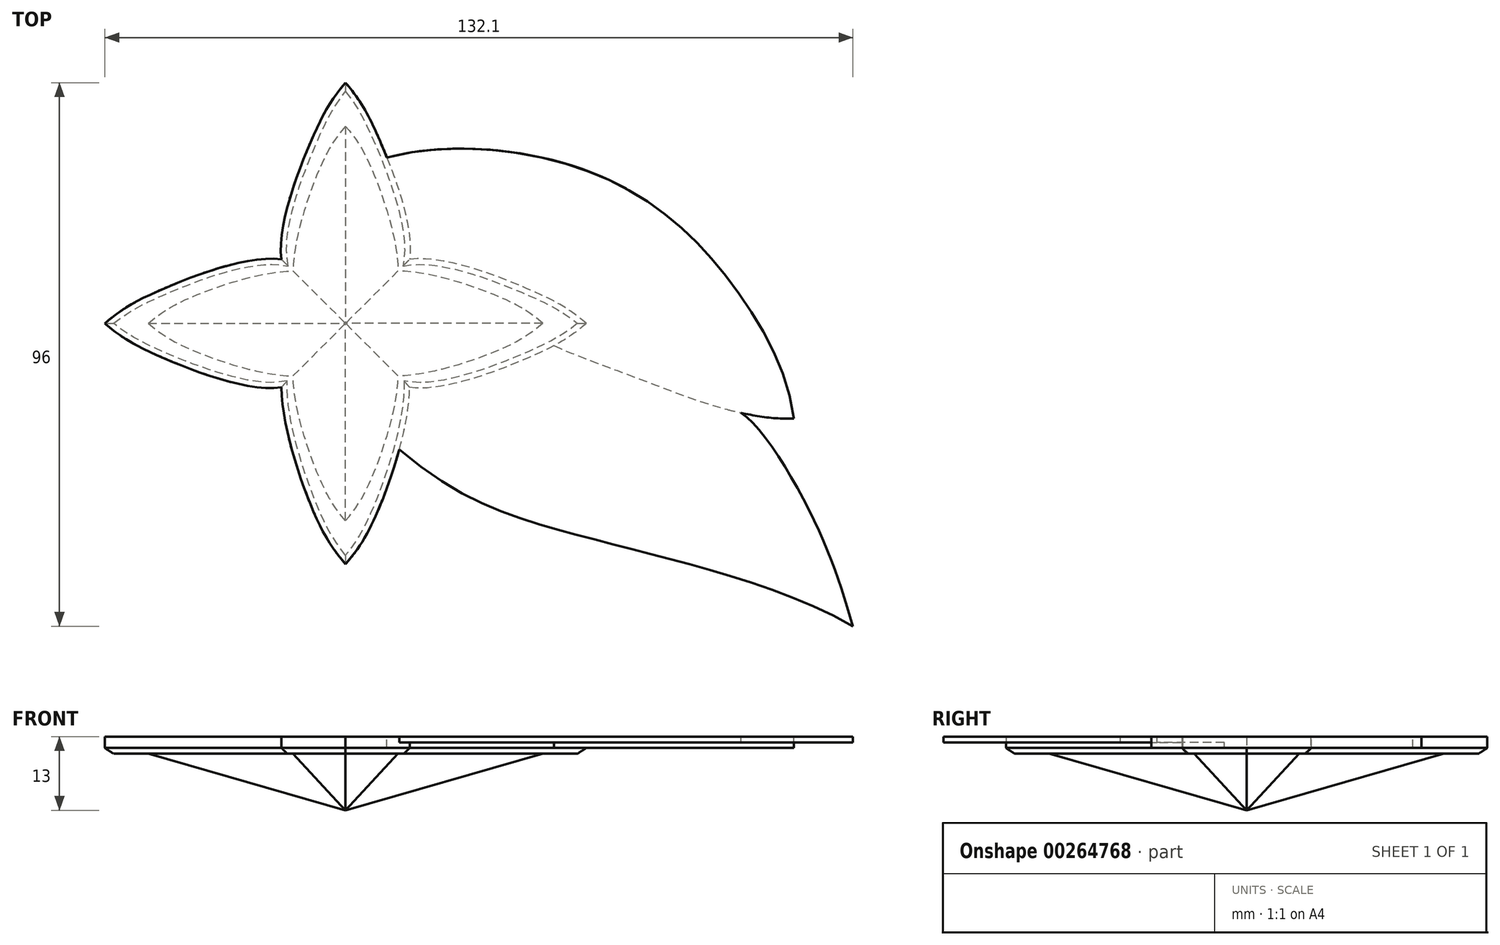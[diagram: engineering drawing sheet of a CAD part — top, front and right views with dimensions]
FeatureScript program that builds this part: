
annotation { "Feature Type Name" : "Feature", "Feature Type Description" : "" }
export const myFeature = defineFeature(function(context is Context, id is Id, definition is map)
    precondition{}
    {
        {
            var Q0;
            Q0=qCreatedBy(makeId("Top.planeOp"),FACE);
            var sketch = newSketch(context, id + "F0", { "sketchPlane" : qUnion([Q0])});
            skLineSegment(sketch, "E0", {"start": v(0, 0) * mm, "end": v(0, 50) * mm});
            skLineSegment(sketch, "E1", {"start": v(0, 0) * mm, "end": v(-50, 0) * mm});
            skFitSpline(sketch, "E2", {"points": [v(0, 50) * mm, v(-50, 0) * mm], "startDerivative": vector(-22.26, -93.04) * mm, "endDerivative": vector(-77.74, -6.96) * mm});
            skFitSpline(sketch, "E3.MirrorCS", {"points": [v(0, 50) * mm, v(50, 0) * mm], "startDerivative": vector(22.26, -93.04) * mm, "endDerivative": vector(77.74, -6.96) * mm});
            skFitSpline(sketch, "E4.MirrorCS", {"points": [v(0, -50) * mm, v(-50, 0) * mm], "startDerivative": vector(-22.26, 93.04) * mm, "endDerivative": vector(-77.74, 6.96) * mm});
            skFitSpline(sketch, "E5.MirrorCS", {"points": [v(0, -50) * mm, v(50, 0) * mm], "startDerivative": vector(22.26, 93.04) * mm, "endDerivative": vector(77.74, 6.96) * mm});
            skSolve(sketch);
        }
        {
            var Q0;
            Q0=qCreatedBy(makeId("Top.planeOp"),FACE);
            var sketch = newSketch(context, id + "F1", { "sketchPlane" : qUnion([Q0])});
            skFitSpline(sketch, "E6", {"points": [v(0, 49.98) * mm, v(-7.34, 30.13) * mm, v(-11.2, 11.2) * mm], "startDerivative": vector(-14.95, -18.4) * mm, "endDerivative": vector(-4.03, -50.51) * mm});
            skFitSpline(sketch, "E7.MirrorCS", {"points": [v(0, 49.98) * mm, v(7.34, 30.13) * mm, v(11.2, 11.2) * mm], "startDerivative": vector(14.95, -18.4) * mm, "endDerivative": vector(4.03, -50.51) * mm});
            skFitSpline(sketch, "E8.MirrorCS", {"points": [v(0, -49.98) * mm, v(-7.34, -30.13) * mm, v(-11.2, -11.2) * mm], "startDerivative": vector(-14.95, 18.4) * mm, "endDerivative": vector(-4.03, 50.51) * mm});
            skFitSpline(sketch, "E9.MirrorCS", {"points": [v(0, -49.98) * mm, v(7.34, -30.13) * mm, v(11.2, -11.2) * mm], "startDerivative": vector(14.95, 18.4) * mm, "endDerivative": vector(4.03, 50.51) * mm});
            skLineSegment(sketch, "E10", {"start": v(-11.2, 11.2) * mm, "end": v(11.2, -11.2) * mm, "construction": true});
            skLineSegment(sketch, "E11", {"start": v(11.2, 11.2) * mm, "end": v(-11.2, -11.2) * mm, "construction": true});
            skFitSpline(sketch, "E12.MirrorCS", {"points": [v(-49.98, 0) * mm, v(-30.13, -7.34) * mm, v(-11.2, -11.2) * mm], "startDerivative": vector(18.4, -14.95) * mm, "endDerivative": vector(50.51, -4.03) * mm});
            skFitSpline(sketch, "E13.MirrorCS", {"points": [v(-49.98, 0) * mm, v(-30.13, 7.34) * mm, v(-11.2, 11.2) * mm], "startDerivative": vector(18.4, 14.95) * mm, "endDerivative": vector(50.51, 4.03) * mm});
            skFitSpline(sketch, "E14.MirrorCS", {"points": [v(49.98, 0) * mm, v(30.13, 7.34) * mm, v(11.2, 11.2) * mm], "startDerivative": vector(-18.4, 14.95) * mm, "endDerivative": vector(-50.51, 4.03) * mm});
            skFitSpline(sketch, "E15.MirrorCS", {"points": [v(49.98, 0) * mm, v(30.13, -7.34) * mm, v(11.2, -11.2) * mm], "startDerivative": vector(-18.4, -14.95) * mm, "endDerivative": vector(-50.51, -4.03) * mm});
            skLineSegment(sketch, "E16", {"start": v(0, 49.98) * mm, "end": v(0, 0) * mm, "construction": true});
            skLineSegment(sketch, "E17", {"start": v(0, 0) * mm, "end": v(0, -49.98) * mm, "construction": true});
            skLineSegment(sketch, "E18", {"start": v(0, 0) * mm, "end": v(49.98, 0) * mm, "construction": true});
            skLineSegment(sketch, "E19", {"start": v(0, 0) * mm, "end": v(-49.98, 0) * mm, "construction": true});
            skSolve(sketch);
        }
        {
            var Q0;
            Q0=qCreatedBy(makeId("Top.planeOp"),FACE);
            cPlane(context, id + "F2", {"entities" : qUnion([Q0]), "cplaneType" : CPlaneType.OFFSET, "offset" : 10 * mm, "width" : 150 * mm, "height" : 150 * mm});
        }
        {
            var Q0;
            Q0=qCreatedBy(id+"F2.planeOp",FACE);
            var sketch = newSketch(context, id + "F3", { "sketchPlane" : qUnion([Q0])});
            skLineSegment(sketch, "E20", {"start": v(0, 0) * mm, "end": v(0, 34.83) * mm, "construction": true});
            skFitSpline(sketch, "E21", {"points": [v(0, 34.83) * mm, v(-5, 26.37) * mm, v(-9.27, 9.27) * mm], "startDerivative": vector(-15.34, -17.47) * mm, "endDerivative": vector(-0.1, -26.43) * mm});
            skFitSpline(sketch, "E22.MirrorCS", {"points": [v(0, 34.83) * mm, v(5, 26.37) * mm, v(9.27, 9.27) * mm], "startDerivative": vector(15.34, -17.47) * mm, "endDerivative": vector(0.1, -26.43) * mm});
            skFitSpline(sketch, "E23.MirrorCS", {"points": [v(0, -34.83) * mm, v(-5, -26.37) * mm, v(-9.27, -9.27) * mm], "startDerivative": vector(-15.34, 17.47) * mm, "endDerivative": vector(-0.1, 26.43) * mm});
            skFitSpline(sketch, "E24.MirrorCS", {"points": [v(0, -34.83) * mm, v(5, -26.37) * mm, v(9.27, -9.27) * mm], "startDerivative": vector(15.34, 17.47) * mm, "endDerivative": vector(0.1, 26.43) * mm});
            skLineSegment(sketch, "E25", {"start": v(-9.27, 9.27) * mm, "end": v(9.27, -9.27) * mm, "construction": true});
            skLineSegment(sketch, "E26", {"start": v(9.27, 9.27) * mm, "end": v(-9.27, -9.27) * mm, "construction": true});
            skFitSpline(sketch, "E27.MirrorCS", {"points": [v(-34.83, 0) * mm, v(-26.37, 5) * mm, v(-9.27, 9.27) * mm], "startDerivative": vector(17.47, 15.34) * mm, "endDerivative": vector(26.43, 0.1) * mm});
            skFitSpline(sketch, "E28.MirrorCS", {"points": [v(-34.83, 0) * mm, v(-26.37, -5) * mm, v(-9.27, -9.27) * mm], "startDerivative": vector(17.47, -15.34) * mm, "endDerivative": vector(26.43, -0.1) * mm});
            skFitSpline(sketch, "E29.MirrorCS", {"points": [v(34.83, 0) * mm, v(26.37, -5) * mm, v(9.27, -9.27) * mm], "startDerivative": vector(-17.47, -15.34) * mm, "endDerivative": vector(-26.43, -0.1) * mm});
            skFitSpline(sketch, "E30.MirrorCS", {"points": [v(34.83, 0) * mm, v(26.37, 5) * mm, v(9.27, 9.27) * mm], "startDerivative": vector(-17.47, 15.34) * mm, "endDerivative": vector(-26.43, 0.1) * mm});
            skSolve(sketch);
        }
        {
            var Q0;
            Q0=makeQuery(id+"F3.imprint","IMPRINT",FACE,{"disambiguationData":[TD([[makeQuery(id+"F3.imprint","IMPRINT",EDGE,{"derivedFrom":sQuery(id+"F3.wireOp",EDGE,"E21")}),1.0]])]});
            var Q1;
            Q1=qCreatedBy(makeId("Origin.pointOp"),VERTEX);
            loft(context, id + "F4", {"sheetProfilesArray" : [{ "sheetProfileEntities" : qUnion([Q0]) }, { "sheetProfileEntities" : qUnion([Q1]) }]});
        }
        {
            var Q0;
            Q0=makeQuery(id+"F4.opLoft","CAP_FACE",FACE,{"disambiguationData":[OSD([makeQuery(id+"F3.imprint","IMPRINT",FACE,{"disambiguationData":[TD([[makeQuery(id+"F3.imprint","IMPRINT",EDGE,{"derivedFrom":sQuery(id+"F3.wireOp",EDGE,"E21")}),1.0]])]})])],"isStart":true});
            var sketch = newSketch(context, id + "F5", { "sketchPlane" : qUnion([Q0])});
            skLineSegment(sketch, "E31", {"start": v(0, 0) * mm, "end": v(0, 42.5) * mm, "construction": true});
            skFitSpline(sketch, "E32", {"points": [v(0, 42.5) * mm, v(-6.1, 32.17) * mm, v(-11.31, 11.31) * mm], "startDerivative": vector(-18.71, -21.32) * mm, "endDerivative": vector(4.19, -29.93) * mm});
            skFitSpline(sketch, "E33.MirrorCS", {"points": [v(0, 42.5) * mm, v(6.1, 32.17) * mm, v(11.31, 11.31) * mm], "startDerivative": vector(18.71, -21.32) * mm, "endDerivative": vector(-4.19, -29.93) * mm});
            skFitSpline(sketch, "E34.MirrorCS", {"points": [v(0, -42.5) * mm, v(-6.1, -32.17) * mm, v(-11.31, -11.31) * mm], "startDerivative": vector(-18.71, 21.32) * mm, "endDerivative": vector(-0.11, 32.25) * mm});
            skFitSpline(sketch, "E35.MirrorCS", {"points": [v(0, -42.5) * mm, v(6.1, -32.17) * mm, v(11.31, -11.31) * mm], "startDerivative": vector(18.71, 21.32) * mm, "endDerivative": vector(0.11, 32.25) * mm});
            skLineSegment(sketch, "E36", {"start": v(-11.31, 11.31) * mm, "end": v(11.31, -11.31) * mm, "construction": true});
            skLineSegment(sketch, "E37", {"start": v(11.31, 11.31) * mm, "end": v(-11.31, -11.31) * mm, "construction": true});
            skFitSpline(sketch, "E38.MirrorCS", {"points": [v(-42.5, 0) * mm, v(-32.17, 6.1) * mm, v(-11.31, 11.31) * mm], "startDerivative": vector(21.32, 18.71) * mm, "endDerivative": vector(29.93, -4.19) * mm});
            skFitSpline(sketch, "E39.MirrorCS", {"points": [v(-42.5, 0) * mm, v(-32.17, -6.1) * mm, v(-11.31, -11.31) * mm], "startDerivative": vector(21.32, -18.71) * mm, "endDerivative": vector(29.93, 4.19) * mm});
            skFitSpline(sketch, "E40.MirrorCS", {"points": [v(42.5, 0) * mm, v(32.17, -6.1) * mm, v(11.31, -11.31) * mm], "startDerivative": vector(-21.32, -18.71) * mm, "endDerivative": vector(-29.93, 4.19) * mm});
            skFitSpline(sketch, "E41.MirrorCS", {"points": [v(42.5, 0) * mm, v(32.17, 6.1) * mm, v(11.31, 11.31) * mm], "startDerivative": vector(-21.32, 18.71) * mm, "endDerivative": vector(-29.93, -4.19) * mm});
            skLineSegment(sketch, "E42", {"start": v(0, -42.5) * mm, "end": v(0, 0) * mm, "construction": true});
            skLineSegment(sketch, "E43", {"start": v(42.5, 0) * mm, "end": v(0, 0) * mm, "construction": true});
            skLineSegment(sketch, "E44", {"start": v(0, 42.5) * mm, "end": v(0, 0) * mm, "construction": true});
            skLineSegment(sketch, "E45", {"start": v(0, 0) * mm, "end": v(-42.5, 0) * mm, "construction": true});
            skSolve(sketch);
        }
        {
            var Q0;
            Q0=makeQuery(id+"F5.imprint","IMPRINT",FACE,{"disambiguationData":[TD([[makeQuery(id+"F5.imprint","IMPRINT",EDGE,{"derivedFrom":sQuery(id+"F5.wireOp",EDGE,"E32")}),1.0]])]});
            var Q1;
            {var subQ2=sQuery(id+"F3.wireOp",EDGE,"E22.MirrorCS");var subQ4=sQuery(id+"F3.wireOp",EDGE,"E27.MirrorCS");var subQ5=sQuery(id+"F3.wireOp",EDGE,"E21");Q1=makeQuery(id+"F5.imprint","IMPRINT",FACE,{"disambiguationData":[TD([[makeQuery(id+"F5.imprint","IMPRINT",EDGE,{"derivedFrom":makeQuery(id+"F4.opLoft","MID_CAP_EDGE",EDGE,{"disambiguationData":[OSD([subQ5,subQ2,subQ4])],"capPos":0.0})}),1.0]])]});}
            extrude(context, id + "F6", {"entities" : qUnion([Q0, Q1]), "operationType" : NewBodyOperationType.ADD, "depth" : 3 * mm, "offsetDistance" : 25 * mm});
        }
        {
            var Q0;
            Q0=makeQuery(id+"F6.opExtrude","CAP_EDGE",EDGE,{"disambiguationData":[OSD([sQuery(id+"F5.wireOp",EDGE,"E34.MirrorCS")])],"isStart":true});
            var Q1;
            Q1=makeQuery(id+"F6.opExtrude","CAP_EDGE",EDGE,{"disambiguationData":[OSD([sQuery(id+"F5.wireOp",EDGE,"E35.MirrorCS")])],"isStart":true});
            var Q2;
            Q2=makeQuery(id+"F6.opExtrude","CAP_EDGE",EDGE,{"disambiguationData":[OSD([sQuery(id+"F5.wireOp",EDGE,"E39.MirrorCS")])],"isStart":true});
            var Q3;
            Q3=makeQuery(id+"F6.opExtrude","CAP_EDGE",EDGE,{"disambiguationData":[OSD([sQuery(id+"F5.wireOp",EDGE,"E38.MirrorCS")])],"isStart":true});
            var Q4;
            Q4=makeQuery(id+"F6.opExtrude","CAP_EDGE",EDGE,{"disambiguationData":[OSD([sQuery(id+"F5.wireOp",EDGE,"E32")])],"isStart":true});
            var Q5;
            Q5=makeQuery(id+"F6.opExtrude","CAP_EDGE",EDGE,{"disambiguationData":[OSD([sQuery(id+"F5.wireOp",EDGE,"E33.MirrorCS")])],"isStart":true});
            var Q6;
            Q6=makeQuery(id+"F6.opExtrude","CAP_EDGE",EDGE,{"disambiguationData":[OSD([sQuery(id+"F5.wireOp",EDGE,"E41.MirrorCS")])],"isStart":true});
            var Q7;
            Q7=makeQuery(id+"F6.opExtrude","CAP_EDGE",EDGE,{"disambiguationData":[OSD([sQuery(id+"F5.wireOp",EDGE,"E40.MirrorCS")])],"isStart":true});
            chamfer(context, id + "F7", {"entities" : qUnion([Q0, Q1, Q2, Q3, Q4, Q5, Q6, Q7]), "width" : 1 * mm, "tangentPropagation" : true});
        }
        {
            var Q0;
            Q0=makeQuery(id+"F6.opExtrude","CAP_FACE",FACE,{"disambiguationData":[OSD([sQuery(id+"F5.wireOp",EDGE,"E32"),sQuery(id+"F5.wireOp",EDGE,"E33.MirrorCS"),sQuery(id+"F5.wireOp",EDGE,"E34.MirrorCS"),sQuery(id+"F5.wireOp",EDGE,"E35.MirrorCS"),sQuery(id+"F5.wireOp",EDGE,"E38.MirrorCS"),sQuery(id+"F5.wireOp",EDGE,"E39.MirrorCS"),sQuery(id+"F5.wireOp",EDGE,"E40.MirrorCS"),sQuery(id+"F5.wireOp",EDGE,"E41.MirrorCS")])],"isStart":false});
            var sketch = newSketch(context, id + "F8", { "sketchPlane" : qUnion([Q0])});
            skFitSpline(sketch, "E46", {"points": [v(9.48, -22.3) * mm, v(37.5, -36.43) * mm, v(61.1, -42.64) * mm, v(89.6, -53.5) * mm], "startDerivative": vector(89.14, -76) * mm, "endDerivative": vector(78.78, -45.1) * mm});
            skFitSpline(sketch, "E47", {"points": [v(89.6, -53.5) * mm, v(85.32, -42.5) * mm, v(71.79, -21.04) * mm, v(61.72, -9.34) * mm, v(42.5, 0) * mm], "startDerivative": vector(-15.1, 42.47) * mm, "endDerivative": vector(-68.38, -18.89) * mm});
            skFitSpline(sketch, "E48", {"points": [v(79.14, -16.82) * mm, v(70.18, 4.23) * mm, v(56.3, 19.38) * mm, v(36.22, 28.94) * mm, v(7.3, 29.31) * mm], "startDerivative": vector(-12.06, 95.22) * mm, "endDerivative": vector(-98.45, -25.93) * mm});
            skFitSpline(sketch, "E49", {"points": [v(36.8, -3.93) * mm, v(52.33, -9.96) * mm, v(79.14, -16.82) * mm], "startDerivative": vector(29.94, -13.56) * mm, "endDerivative": vector(46.73, 1.64) * mm});
            skFitSpline(sketch, "E50", {"points": [v(89.6, -53.5) * mm, v(82.56, -34.43) * mm, v(69.83, -15.8) * mm], "startDerivative": vector(-11.94, 39.85) * mm, "endDerivative": vector(-22.36, 14.68) * mm});
            skSolve(sketch);
        }
        {
            var Q0;
            {var subQ1=sQuery(id+"F8.wireOp",EDGE,"E48");Q0=makeQuery(id+"F8.imprint","IMPRINT",FACE,{"disambiguationData":[TD([[makeQuery(id+"F8.imprint","IMPRINT",EDGE,{"derivedFrom":subQ1}),1.0]])]});}
            var Q1;
            {var subQ0=sQuery(id+"F8.wireOp",EDGE,"1be1860b-0cd8-4775-8853-f19aa7d13203");var subQ1=sQuery(id+"F8.wireOp",EDGE,"E47");var subQ3=makeQuery(id+"F8.imprint","INTERSECT",VERTEX,{"derivedFrom":[subQ1,subQ0]});Q1=makeQuery(id+"F8.imprint","IMPRINT",FACE,{"disambiguationData":[TD([[makeQuery(id+"F8.imprint","IMPRINT",EDGE,{"disambiguationData":[TD([[subQ3,-1.0]])],"derivedFrom":subQ1}),1.0]])]});}
            extrude(context, id + "F9", {"entities" : qUnion([Q0, Q1]), "operationType" : NewBodyOperationType.ADD, "oppositeDirection" : true, "depth" : 2 * mm, "offsetDistance" : 25 * mm});
        }
        {
            var Q0;
            {var subQ4=sQuery(id+"F8.wireOp",EDGE,"E46");Q0=makeQuery(id+"F8.imprint","IMPRINT",FACE,{"disambiguationData":[TD([[makeQuery(id+"F8.imprint","IMPRINT",EDGE,{"derivedFrom":subQ4}),1.0]])]});}
            var Q1;
            {var subQ0=sQuery(id+"F8.wireOp",EDGE,"E50");Q1=makeQuery(id+"F8.imprint","IMPRINT",FACE,{"disambiguationData":[TD([[makeQuery(id+"F8.imprint","IMPRINT",EDGE,{"derivedFrom":subQ0}),1.0]])]});}
            extrude(context, id + "F10", {"entities" : qUnion([Q0, Q1]), "operationType" : NewBodyOperationType.ADD, "oppositeDirection" : true, "depth" : 1 * mm, "offsetDistance" : 25 * mm});
        }
    });
